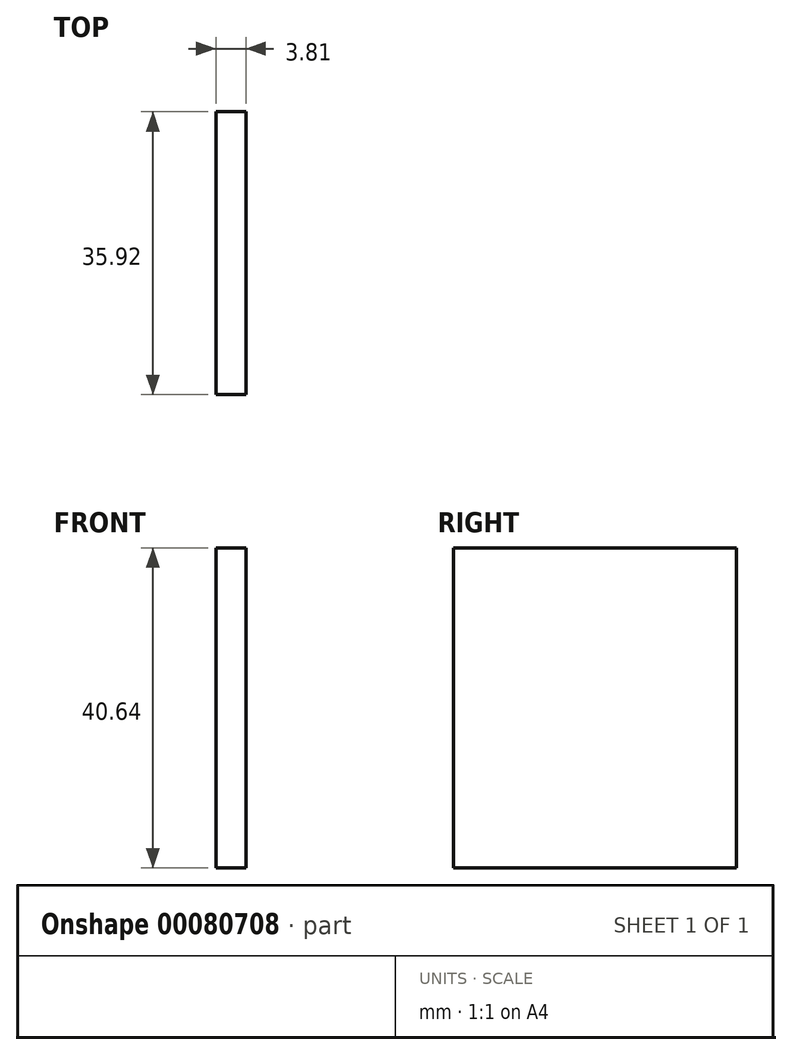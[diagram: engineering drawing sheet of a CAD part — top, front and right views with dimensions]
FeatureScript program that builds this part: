
annotation { "Feature Type Name" : "Feature", "Feature Type Description" : "" }
export const myFeature = defineFeature(function(context is Context, id is Id, definition is map)
    precondition{}
    {
        {
            var Q0;
            Q0=qCreatedBy(makeId("Right.planeOp"),FACE);
            var sketch = newSketch(context, id + "F0", { "sketchPlane" : qUnion([Q0])});
            skLineSegment(sketch, "E0.bottom", {"start": v(17.96, -20.32) * mm, "end": v(-17.96, -20.32) * mm});
            skLineSegment(sketch, "E0.top", {"start": v(17.96, 20.32) * mm, "end": v(-17.96, 20.32) * mm});
            skLineSegment(sketch, "E0.left", {"start": v(17.96, -20.32) * mm, "end": v(17.96, 20.32) * mm});
            skLineSegment(sketch, "E0.right", {"start": v(-17.96, -20.32) * mm, "end": v(-17.96, 20.32) * mm});
            skPoint(sketch, "E0.middle", {"position": v(0, 0) * mm});
            skSolve(sketch);
        }
        {
            var Q0;
            Q0=makeQuery(id+"F0.imprint","IMPRINT",FACE,{"disambiguationData":[TD([[makeQuery(id+"F0.imprint","IMPRINT",EDGE,{"derivedFrom":sQuery(id+"F0.wireOp",EDGE,"E0.bottom")}),-1.0]])]});
            extrude(context, id + "F1", {"entities" : qUnion([Q0]), "depth" : 3.8 * mm});
        }
    });
